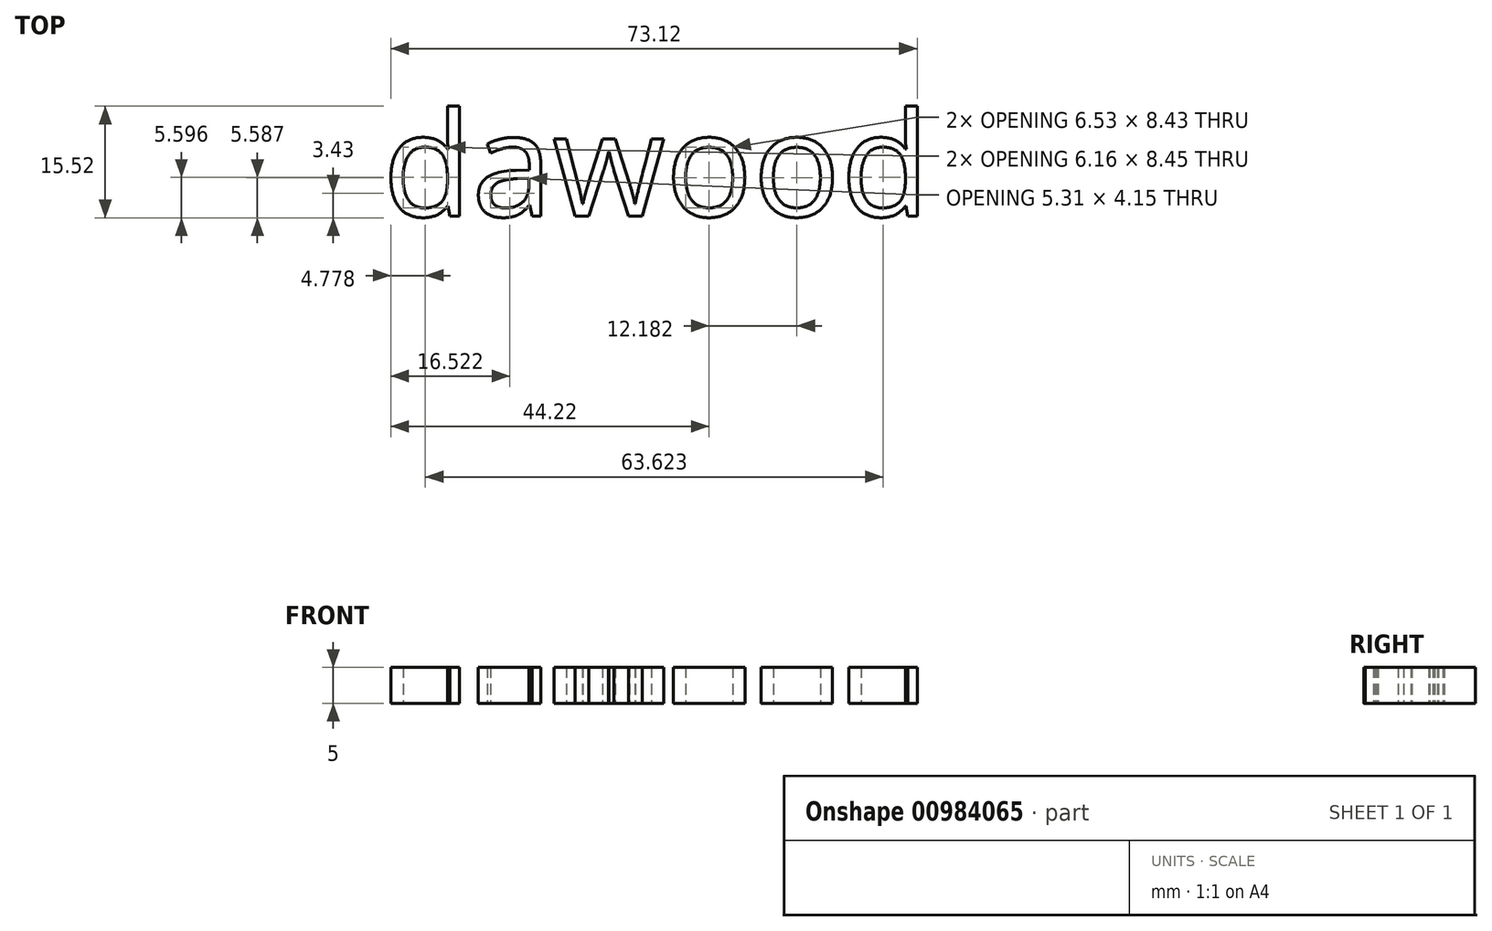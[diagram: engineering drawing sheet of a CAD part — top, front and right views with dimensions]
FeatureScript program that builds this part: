
annotation { "Feature Type Name" : "Feature", "Feature Type Description" : "" }
export const myFeature = defineFeature(function(context is Context, id is Id, definition is map)
    precondition{}
    {
        {
            var Q0;
            Q0=qCreatedBy(makeId("Top.planeOp"),FACE);
            var sketch = newSketch(context, id + "F0", { "sketchPlane" : qUnion([Q0])});
            skText(sketch, "E0", { "text": "dawood", "fontName": "OpenSans-Regular.ttf"});
            const initialGuessF0  = {"E0": [0, 0, 1, 0, 0.01452]};
            skSetInitialGuess(sketch, initialGuessF0);
            skSolve(sketch);
        }
        {
            var Q0;
            Q0 = qSketchRegion(id + "F0", true);
            extrude(context, id + "F1", {"entities" : qUnion([Q0]), "depth" : 5 * mm, "offsetDistance" : 25 * mm});
        }
    });
